# Revit family: Sink-Pedestal-Lavatory-KOHLER-PORTRAIT-K-2221T_1
name_source: partatom
category: Plumbing Fixtures
revit_build: Autodesk Revit 2017 (Build: 20160225_1515(x64)
units: mm (PartAtom-declared; Revit-internal decimal feet)

## family parameters
Cut with Voids When Loaded = No
Host = Face
OmniClass Number = 23.31.13.00
OmniClass Title = Sinks
Part Type = Normal
Room Calculation Point = No
Round Connector Dimension = Use Diameter
Shared = No

## types (3) — shared parameters
ADA Compliant = No
Assembly Code = D2010400
CW Connection = No
Cold Water Inlet = Cold Water Inlet
Date Modified = 04/27/2020
Default Elevation = 0"
Description = PEDESTAL LAV, 1-H
Drain Included = No
Finish = Kohler-Vitreous_China-0-White
HW Connection = No
Height = 36 11/16"
Hot Water Inlet = Hot Water Inlet
Length = 19 5/16"
Manufacturer = KOHLER Co.
MasterFormat 1995 = 15410
MasterFormat 2004 = 22.41.16
Material = Vitreous China
Product Documentation Link = http://files.kohler.com.cn
Product Name = PORTRAIT
Product Page URL = http://www.kohler.com.cn
URL = http://www.kohler.com.cn
Vent Connection = No
Waste Connection = Yes
Waste Water Outlet = Waste Water Outlet
WaterSense Certified = No
Width = 27 1/4"

## per-type parameters (varying)
| type | 4 inch Faucet Hole | 8 inch Faucet Hole | Faucet Hole Spacing | Model | Single Faucet Hole | Type |
| Single Faucet Hole, 0-White | No | No | 0" | K-2221T-1-0 | Yes | 1 |
| 4 inch Centerset Faucet Holes, 0-White | Yes | No | 4" | K-2221T-4-0 | No | 2 |
| 8 inch Centerset Faucet Holes, 0-White | No | Yes | 8 1/16" | K-2221T-8-0 | No | 3 |

## geometry (parser evidence)
native form markers: Sweep x4
no freeform markers — native parametric forms only
